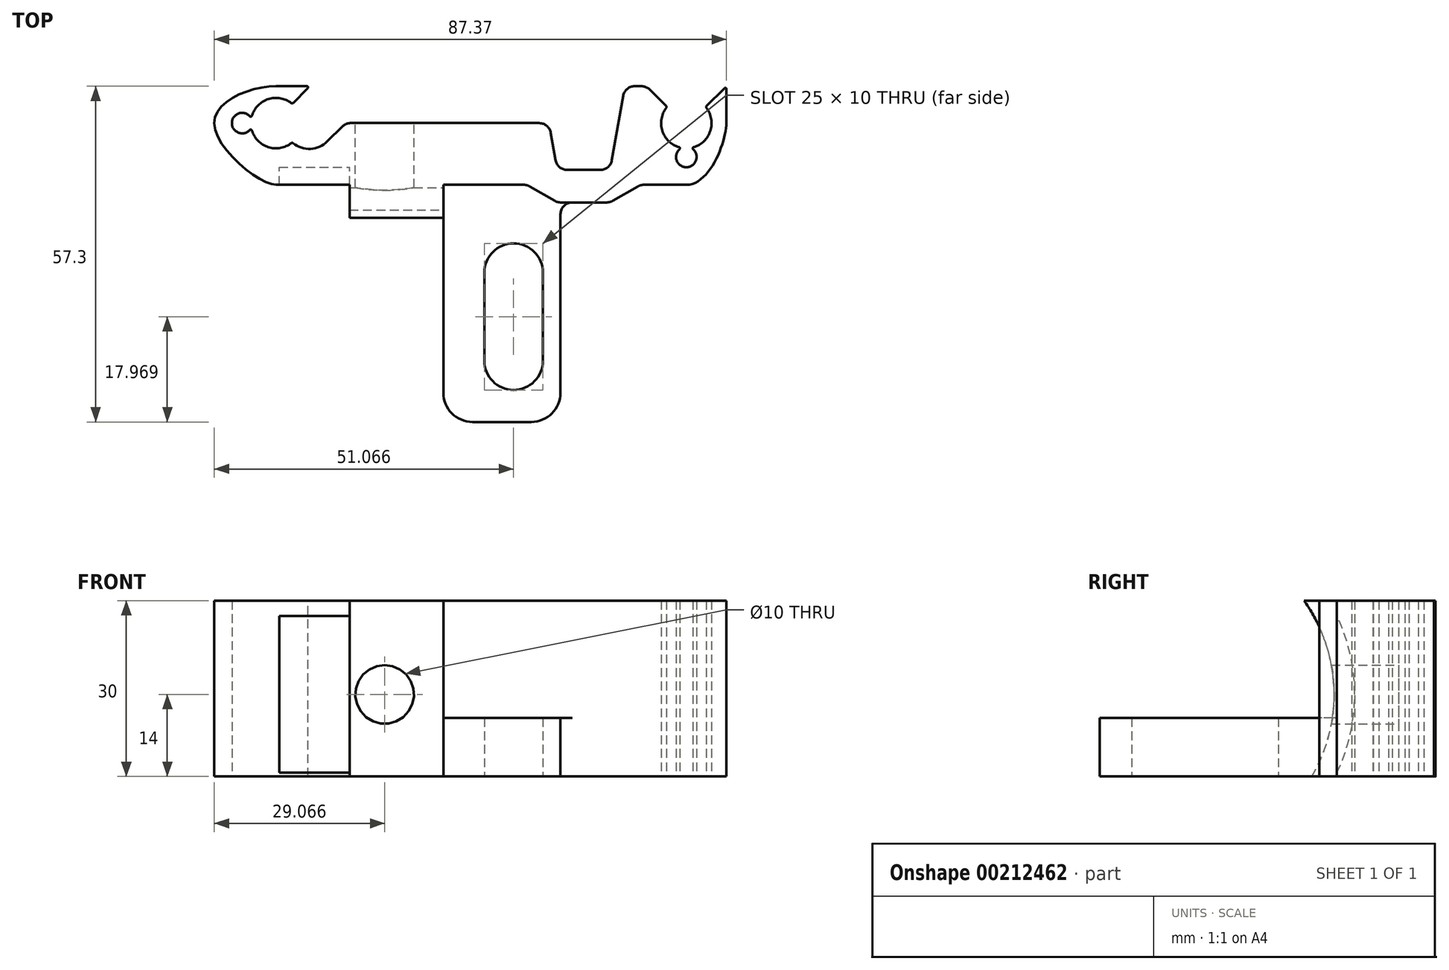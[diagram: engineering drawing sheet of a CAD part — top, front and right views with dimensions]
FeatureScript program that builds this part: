
annotation { "Feature Type Name" : "Feature", "Feature Type Description" : "" }
export const myFeature = defineFeature(function(context is Context, id is Id, definition is map)
    precondition{}
    {
        {
            var Q0;
            Q0=qCreatedBy(makeId("Top.planeOp"),FACE);
            var sketch = newSketch(context, id + "F0", { "sketchPlane" : qUnion([Q0])});
            skCircle(sketch, "E0", {"center": v(0, 0) * mm, "radius": 4.3 * mm});
            skCircle(sketch, "E1", {"center": v(5.67, 0) * mm, "radius": 4.4 * mm});
            skLineSegment(sketch, "E2", {"start": v(2.76, 3.3) * mm, "end": v(2.76, -3.3) * mm, "construction": true});
            skCircle(sketch, "E3", {"center": v(-5.78, 0) * mm, "radius": 1.75 * mm});
            skLineSegment(sketch, "E4", {"start": v(-4.22, 0.8) * mm, "end": v(-4.22, -0.8) * mm, "construction": true});
            skCircle(sketch, "E5", {"center": v(70, 0) * mm, "radius": 4.3 * mm});
            skLineSegment(sketch, "E6", {"start": v(0, 6.3) * mm, "end": v(63.16, 6.3) * mm});
            skLineSegment(sketch, "E7", {"start": v(0, -10.53) * mm, "end": v(70, -10.53) * mm});
            skFitSpline(sketch, "E8", {"points": [v(0, 6.3) * mm, v(-10.53, 0) * mm, v(0, -10.53) * mm], "startDerivative": vector(-26.26, 0) * mm, "endDerivative": vector(16.05, 0) * mm});
            skLineSegment(sketch, "E9", {"start": v(-10.53, 0) * mm, "end": v(-10.53, 6.3) * mm, "construction": true});
            skLineSegment(sketch, "E10", {"start": v(2.76, 3.3) * mm, "end": v(5.76, 6.3) * mm});
            skLineSegment(sketch, "E11", {"start": v(8.78, -3.11) * mm, "end": v(18.19, 6.3) * mm});
            skLineSegment(sketch, "E12", {"start": v(66.7, 2.76) * mm, "end": v(73.3, 2.76) * mm, "construction": true});
            skLineSegment(sketch, "E13", {"start": v(70, 0) * mm, "end": v(70, -10.53) * mm, "construction": true});
            skCircle(sketch, "E14", {"center": v(70, -5.78) * mm, "radius": 1.75 * mm});
            skLineSegment(sketch, "E15", {"start": v(69.2, -4.22) * mm, "end": v(70.8, -4.22) * mm, "construction": true});
            skLineSegment(sketch, "E16", {"start": v(73.3, 2.76) * mm, "end": v(76.84, 6.3) * mm});
            skLineSegment(sketch, "E17", {"start": v(76.84, 6.3) * mm, "end": v(76.84, 0) * mm});
            skFitSpline(sketch, "E18", {"points": [v(76.84, 0) * mm, v(70, -10.53) * mm, v(59.47, 0) * mm], "startDerivative": vector(0, -18.6) * mm, "endDerivative": vector(0, 8.99) * mm});
            skLineSegment(sketch, "E19", {"start": v(0, -4.3) * mm, "end": v(0, -10.53) * mm, "construction": true});
            skLineSegment(sketch, "E20", {"start": v(59.47, 0) * mm, "end": v(65.7, 0) * mm, "construction": true});
            skLineSegment(sketch, "E21", {"start": v(66.7, 2.76) * mm, "end": v(63.16, 6.3) * mm});
            skPoint(sketch, "E22.orphan", {"position": v(70, 6.3) * mm});
            skLineSegment(sketch, "E23", {"start": v(45.48, 6.3) * mm, "end": v(48, -8) * mm});
            skLineSegment(sketch, "E24", {"start": v(48, -8) * mm, "end": v(57, -8) * mm});
            skLineSegment(sketch, "E25", {"start": v(57, -8) * mm, "end": v(59.52, 6.3) * mm});
            skLineSegment(sketch, "E26", {"start": v(11.89, 0) * mm, "end": v(46.59, 0) * mm});
            skLineSegment(sketch, "E27", {"start": v(42.8, -10.53) * mm, "end": v(48, -13.53) * mm});
            skLineSegment(sketch, "E28", {"start": v(48, -13.53) * mm, "end": v(57, -13.53) * mm});
            skLineSegment(sketch, "E29", {"start": v(57, -13.53) * mm, "end": v(62.2, -10.53) * mm});
            skSolve(sketch);
        }
        {
            var Q0;
            {var subQ18=sQuery(id+"F0.wireOp",EDGE,"E7");Q0=makeQuery(id+"F0.imprint","IMPRINT",FACE,{"disambiguationData":[TD([[makeQuery(id+"F0.imprint","IMPRINT",EDGE,{"derivedFrom":subQ18}),1.0]])]});}
            var Q1;
            {var subQ0=sQuery(id+"F0.wireOp",EDGE,"E27");Q1=makeQuery(id+"F0.imprint","IMPRINT",FACE,{"disambiguationData":[TD([[makeQuery(id+"F0.imprint","IMPRINT",EDGE,{"derivedFrom":subQ0}),1.0]])]});}
            extrude(context, id + "F1", {"entities" : qUnion([Q0, Q1]), "depth" : 30 * mm});
        }
        {
            var Q0;
            Q0=makeQuery(id+"F1.opExtrude","SWEPT_EDGE",EDGE,{"disambiguationData":[OSD([sQuery(id+"F0.wireOp",EDGE,"E6"),sQuery(id+"F0.wireOp",EDGE,"E10")])]});
            var Q1;
            Q1=makeQuery(id+"F1.opExtrude","SWEPT_EDGE",EDGE,{"disambiguationData":[OSD([sQuery(id+"F0.wireOp",EDGE,"E0"),sQuery(id+"F0.wireOp",EDGE,"E1"),sQuery(id+"F0.wireOp",EDGE,"E10")])]});
            var Q2;
            {var subQ0=sQuery(id+"F0.wireOp",EDGE,"E3");var subQ1=sQuery(id+"F0.wireOp",EDGE,"E0");Q2=makeQuery(id+"F1.opExtrude","SWEPT_EDGE",EDGE,{"disambiguationData":[OSD([subQ1,subQ0]),TDD([makeQuery(id+"F0.imprint","INTERSECT",VERTEX,{"disambiguationData":[OD(0.0)],"derivedFrom":[subQ1,subQ0]})])]});}
            var Q3;
            {var subQ0=sQuery(id+"F0.wireOp",EDGE,"E3");var subQ1=sQuery(id+"F0.wireOp",EDGE,"E0");Q3=makeQuery(id+"F1.opExtrude","SWEPT_EDGE",EDGE,{"disambiguationData":[OSD([subQ1,subQ0]),TDD([makeQuery(id+"F0.imprint","INTERSECT",VERTEX,{"disambiguationData":[OD(1.0)],"derivedFrom":[subQ1,subQ0]})])]});}
            var Q4;
            Q4=makeQuery(id+"F1.opExtrude","SWEPT_EDGE",EDGE,{"disambiguationData":[OSD([sQuery(id+"F0.wireOp",EDGE,"E0"),sQuery(id+"F0.wireOp",EDGE,"E1")])]});
            var Q5;
            Q5=makeQuery(id+"F1.opExtrude","SWEPT_EDGE",EDGE,{"disambiguationData":[OSD([sQuery(id+"F0.wireOp",EDGE,"E16"),sQuery(id+"F0.wireOp",EDGE,"E17")])]});
            var Q6;
            Q6=makeQuery(id+"F1.opExtrude","SWEPT_EDGE",EDGE,{"disambiguationData":[OSD([sQuery(id+"F0.wireOp",EDGE,"E5"),sQuery(id+"F0.wireOp",EDGE,"E21")])]});
            var Q7;
            {var subQ0=sQuery(id+"F0.wireOp",EDGE,"E14");var subQ1=sQuery(id+"F0.wireOp",EDGE,"E5");Q7=makeQuery(id+"F1.opExtrude","SWEPT_EDGE",EDGE,{"disambiguationData":[OSD([subQ1,subQ0]),TDD([makeQuery(id+"F0.imprint","INTERSECT",VERTEX,{"disambiguationData":[OD(0.0)],"derivedFrom":[subQ1,subQ0]})])]});}
            var Q8;
            {var subQ0=sQuery(id+"F0.wireOp",EDGE,"E14");var subQ1=sQuery(id+"F0.wireOp",EDGE,"E5");Q8=makeQuery(id+"F1.opExtrude","SWEPT_EDGE",EDGE,{"disambiguationData":[OSD([subQ1,subQ0]),TDD([makeQuery(id+"F0.imprint","INTERSECT",VERTEX,{"disambiguationData":[OD(1.0)],"derivedFrom":[subQ1,subQ0]})])]});}
            var Q9;
            Q9=makeQuery(id+"F1.opExtrude","SWEPT_EDGE",EDGE,{"disambiguationData":[OSD([sQuery(id+"F0.wireOp",EDGE,"E5"),sQuery(id+"F0.wireOp",EDGE,"E16")])]});
            fillet(context, id + "F2", {"entities" : qUnion([Q0, Q1, Q2, Q3, Q4, Q5, Q6, Q7, Q8, Q9]), "radius" : .2 * mm, "tangentPropagation" : true, "allowEdgeOverflow" : false});
        }
        {
            var Q0;
            Q0=makeQuery(id+"F1.opExtrude","SWEPT_EDGE",EDGE,{"disambiguationData":[OSD([sQuery(id+"F0.wireOp",EDGE,"E6"),sQuery(id+"F0.wireOp",EDGE,"E21")])]});
            var Q1;
            Q1=makeQuery(id+"F1.opExtrude","SWEPT_EDGE",EDGE,{"disambiguationData":[OSD([sQuery(id+"F0.wireOp",EDGE,"E23"),sQuery(id+"F0.wireOp",EDGE,"E24")])]});
            var Q2;
            Q2=makeQuery(id+"F1.opExtrude","SWEPT_EDGE",EDGE,{"disambiguationData":[OSD([sQuery(id+"F0.wireOp",EDGE,"E6"),sQuery(id+"F0.wireOp",EDGE,"E25")])]});
            var Q3;
            Q3=makeQuery(id+"F1.opExtrude","SWEPT_EDGE",EDGE,{"disambiguationData":[OSD([sQuery(id+"F0.wireOp",EDGE,"E23"),sQuery(id+"F0.wireOp",EDGE,"E26")])]});
            var Q4;
            Q4=makeQuery(id+"F1.opExtrude","SWEPT_EDGE",EDGE,{"disambiguationData":[OSD([sQuery(id+"F0.wireOp",EDGE,"E23"),sQuery(id+"F0.wireOp",EDGE,"E24")])]});
            var Q5;
            Q5=makeQuery(id+"F1.opExtrude","SWEPT_EDGE",EDGE,{"disambiguationData":[OSD([sQuery(id+"F0.wireOp",EDGE,"E24"),sQuery(id+"F0.wireOp",EDGE,"E25")])]});
            var Q6;
            Q6=makeQuery(id+"F1.opExtrude","SWEPT_EDGE",EDGE,{"disambiguationData":[OSD([sQuery(id+"F0.wireOp",EDGE,"E6"),sQuery(id+"F0.wireOp",EDGE,"E21")])]});
            var Q7;
            Q7=makeQuery(id+"F1.opExtrude","SWEPT_EDGE",EDGE,{"disambiguationData":[OSD([sQuery(id+"F0.wireOp",EDGE,"E6"),sQuery(id+"F0.wireOp",EDGE,"E25")])]});
            var Q8;
            Q8=makeQuery(id+"F1.opExtrude","SWEPT_EDGE",EDGE,{"disambiguationData":[OSD([sQuery(id+"F0.wireOp",EDGE,"E11"),sQuery(id+"F0.wireOp",EDGE,"E26")])]});
            var Q9;
            Q9=makeQuery(id+"F1.opExtrude","SWEPT_EDGE",EDGE,{"disambiguationData":[OSD([sQuery(id+"F0.wireOp",EDGE,"E7"),sQuery(id+"F0.wireOp",EDGE,"E27")])]});
            var Q10;
            Q10=makeQuery(id+"F1.opExtrude","SWEPT_EDGE",EDGE,{"disambiguationData":[OSD([sQuery(id+"F0.wireOp",EDGE,"E27"),sQuery(id+"F0.wireOp",EDGE,"E28")])]});
            var Q11;
            Q11=makeQuery(id+"F1.opExtrude","SWEPT_EDGE",EDGE,{"disambiguationData":[OSD([sQuery(id+"F0.wireOp",EDGE,"E28"),sQuery(id+"F0.wireOp",EDGE,"E29")])]});
            var Q12;
            Q12=makeQuery(id+"F1.opExtrude","SWEPT_EDGE",EDGE,{"disambiguationData":[OSD([sQuery(id+"F0.wireOp",EDGE,"E7"),sQuery(id+"F0.wireOp",EDGE,"E29")])]});
            fillet(context, id + "F3", {"entities" : qUnion([Q0, Q1, Q2, Q3, Q4, Q5, Q6, Q7, Q8, Q9, Q10, Q11, Q12]), "radius" : 2 * mm, "tangentPropagation" : true, "allowEdgeOverflow" : false});
        }
        {
            var Q0;
            Q0=makeQuery(id+"F1.opExtrude","CAP_FACE",FACE,{"disambiguationData":[OSD([sQuery(id+"F0.wireOp",EDGE,"E0"),sQuery(id+"F0.wireOp",EDGE,"E1"),sQuery(id+"F0.wireOp",EDGE,"E3"),sQuery(id+"F0.wireOp",EDGE,"E5"),sQuery(id+"F0.wireOp",EDGE,"E6"),sQuery(id+"F0.wireOp",EDGE,"E7"),sQuery(id+"F0.wireOp",EDGE,"E8"),sQuery(id+"F0.wireOp",EDGE,"E10"),sQuery(id+"F0.wireOp",EDGE,"E11"),sQuery(id+"F0.wireOp",EDGE,"E14"),sQuery(id+"F0.wireOp",EDGE,"E16"),sQuery(id+"F0.wireOp",EDGE,"E17"),sQuery(id+"F0.wireOp",EDGE,"E18"),sQuery(id+"F0.wireOp",EDGE,"E21"),sQuery(id+"F0.wireOp",EDGE,"E23"),sQuery(id+"F0.wireOp",EDGE,"E24"),sQuery(id+"F0.wireOp",EDGE,"E25"),sQuery(id+"F0.wireOp",EDGE,"E26"),sQuery(id+"F0.wireOp",EDGE,"E27"),sQuery(id+"F0.wireOp",EDGE,"E28"),sQuery(id+"F0.wireOp",EDGE,"E29")])],"isStart":true});
            var sketch = newSketch(context, id + "F4", { "sketchPlane" : qUnion([Q0])});
            skLineSegment(sketch, "E30.bottom", {"start": v(28.54, 10.53) * mm, "end": v(48.54, 10.53) * mm});
            skLineSegment(sketch, "E30.top", {"start": v(28.54, 51) * mm, "end": v(48.54, 51) * mm});
            skLineSegment(sketch, "E30.left", {"start": v(28.54, 10.53) * mm, "end": v(28.54, 51) * mm});
            skLineSegment(sketch, "E30.right", {"start": v(48.54, 10.53) * mm, "end": v(48.54, 51) * mm});
            skArc(sketch, "E31", {"start": v(45.54, 40.53) * mm, "mid": v(40.54, 45.53) * mm, "end": v(35.54, 40.53) * mm});
            skArc(sketch, "E32", {"start": v(35.54, 25.53) * mm, "mid": v(40.54, 20.53) * mm, "end": v(45.54, 25.53) * mm});
            skLineSegment(sketch, "E33", {"start": v(35.54, 40.53) * mm, "end": v(35.54, 25.53) * mm});
            skLineSegment(sketch, "E34", {"start": v(45.54, 25.53) * mm, "end": v(45.54, 40.53) * mm});
            skSolve(sketch);
        }
        {
            var Q0;
            {var subQ6=sQuery(id+"F4.wireOp",EDGE,"E30.top");Q0=makeQuery(id+"F4.imprint","IMPRINT",FACE,{"disambiguationData":[TD([[makeQuery(id+"F4.imprint","IMPRINT",EDGE,{"derivedFrom":subQ6}),-1.0]])]});}
            extrude(context, id + "F5", {"entities" : qUnion([Q0]), "operationType" : NewBodyOperationType.ADD, "oppositeDirection" : true, "depth" : 10 * mm});
        }
        {
            var Q0;
            Q0=makeQuery(id+"F5.opExtrude","SWEPT_FACE",FACE,{"disambiguationData":[OSD([sQuery(id+"F4.wireOp",EDGE,"E30.left")])]});
            cPlane(context, id + "F6", {"entities" : qUnion([Q0]), "cplaneType" : CPlaneType.OFFSET, "offset" : 10 * mm, "width" : 150 * mm, "height" : 150 * mm});
        }
        {
            var Q0;
            Q0=qCreatedBy(id+"F6.planeOp",FACE);
            var sketch = newSketch(context, id + "F7", { "sketchPlane" : qUnion([Q0])});
            skCircle(sketch, "E35", {"center": v(38.5, 14) * mm, "radius": 27.5 * mm});
            skLineSegment(sketch, "E36", {"start": v(14.83, 0) * mm, "end": v(10.53, 0) * mm});
            skLineSegment(sketch, "E37", {"start": v(10.53, 0) * mm, "end": v(10.53, 30) * mm});
            skLineSegment(sketch, "E38", {"start": v(10.53, 30) * mm, "end": v(16.13, 30) * mm});
            skSolve(sketch);
        }
        {
            var Q0;
            {var subQ0=sQuery(id+"F7.wireOp",EDGE,"E36");Q0=makeQuery(id+"F7.imprint","IMPRINT",FACE,{"disambiguationData":[TD([[makeQuery(id+"F7.imprint","IMPRINT",EDGE,{"derivedFrom":subQ0}),-1.0]])]});}
            var Q1;
            Q1=makeQuery(id+"F5.opExtrude","SWEPT_FACE",FACE,{"disambiguationData":[OSD([sQuery(id+"F4.wireOp",EDGE,"E30.left")])]});
            extrude(context, id + "F8", {"entities" : qUnion([Q0]), "operationType" : NewBodyOperationType.ADD, "depth" : 6 * mm, "hasSecondDirection" : true, "secondDirectionBound" : SecondDirectionBoundingType.UP_TO_SURFACE, "secondDirectionOppositeDirection" : true, "secondDirectionBoundEntityFace" : qUnion([Q1]), "secondDirectionDepth" : 25 * mm});
        }
        {
            var Q0;
            Q0=makeQuery(id+"F8.opExtrude","CAP_FACE",FACE,{"disambiguationData":[OSD([sQuery(id+"F7.wireOp",EDGE,"E35"),sQuery(id+"F7.wireOp",EDGE,"E36"),sQuery(id+"F7.wireOp",EDGE,"E37"),sQuery(id+"F7.wireOp",EDGE,"E38")])],"isStart":false});
            var sketch = newSketch(context, id + "F9", { "sketchPlane" : qUnion([Q0])});
            skCircle(sketch, "E39", {"center": v(38.5, 14) * mm, "radius": 31 * mm});
            skLineSegment(sketch, "E40", {"start": v(10.53, 27.37) * mm, "end": v(10.53, 0.63) * mm});
            skSolve(sketch);
        }
        {
            var Q0;
            {var subQ0=sQuery(id+"F9.wireOp",EDGE,"E40");Q0=makeQuery(id+"F9.imprint","IMPRINT",FACE,{"disambiguationData":[TD([[makeQuery(id+"F9.imprint","IMPRINT",EDGE,{"derivedFrom":subQ0}),1.0]])]});}
            extrude(context, id + "F10", {"entities" : qUnion([Q0]), "operationType" : NewBodyOperationType.REMOVE, "depth" : 12 * mm});
        }
        {
            var Q0;
            {var subQ0=sQuery(id+"F0.wireOp",EDGE,"E7");Q0=makeQuery(id+"F1.opExtrude","SWEPT_FACE",FACE,{"disambiguationData":[OSD([subQ0]),TDD([makeQuery(id+"F0.imprint","IMPRINT",EDGE,{"disambiguationData":[TD([[makeQuery(id+"F0.imprint","INTERSECT",VERTEX,{"derivedFrom":[subQ0,sQuery(id+"F0.wireOp",EDGE,"E8")]}),-1.0]])],"derivedFrom":subQ0})])]});}
            var sketch = newSketch(context, id + "F11", { "sketchPlane" : qUnion([Q0])});
            skCircle(sketch, "E41", {"center": v(18.54, 14) * mm, "radius": 5 * mm});
            skSolve(sketch);
        }
        {
            var Q0;
            Q0=makeQuery(id+"F11.imprint","IMPRINT",FACE,{"disambiguationData":[TD([[makeQuery(id+"F11.imprint","IMPRINT",EDGE,{"derivedFrom":sQuery(id+"F11.wireOp",EDGE,"E41")}),1.0]])]});
            extrude(context, id + "F12", {"entities" : qUnion([Q0]), "operationType" : NewBodyOperationType.REMOVE, "endBound" : BoundingType.THROUGH_ALL, "depth" : 25 * mm, "hasSecondDirection" : true, "secondDirectionBound" : SecondDirectionBoundingType.THROUGH_ALL, "secondDirectionOppositeDirection" : true, "secondDirectionDepth" : 25 * mm});
        }
        {
            var Q0;
            {var subQ0=sQuery(id+"F0.wireOp",EDGE,"E28");var subQ1=sQuery(id+"F0.wireOp",EDGE,"E27");Q0=makeQuery(id+"F5.boolean.opBoolean","MERGE",EDGE,{"derivedFrom":[makeQuery(id+"F3.opFillet","BLEND_EDGE",EDGE,{"blendedFrom":[makeQuery(id+"F1.opExtrude","SWEPT_EDGE",EDGE,{"disambiguationData":[OSD([subQ1,subQ0])]}),makeQuery(id+"F1.opExtrude","SWEPT_FACE",FACE,{"disambiguationData":[OSD([subQ0])]})],"blendedInto":[makeQuery(id+"F1.opExtrude","SWEPT_FACE",FACE,{"disambiguationData":[OSD([subQ0])]})]}),makeQuery(id+"F5.opExtrude","SWEPT_EDGE",EDGE,{"disambiguationData":[OSD([sQuery(id+"F0.wireOp",EDGE,"E0"),sQuery(id+"F0.wireOp",EDGE,"E1"),sQuery(id+"F0.wireOp",EDGE,"E3"),sQuery(id+"F0.wireOp",EDGE,"E5"),sQuery(id+"F0.wireOp",EDGE,"E6"),sQuery(id+"F0.wireOp",EDGE,"E7"),sQuery(id+"F0.wireOp",EDGE,"E8"),sQuery(id+"F0.wireOp",EDGE,"E10"),sQuery(id+"F0.wireOp",EDGE,"E11"),sQuery(id+"F0.wireOp",EDGE,"E14"),sQuery(id+"F0.wireOp",EDGE,"E16"),sQuery(id+"F0.wireOp",EDGE,"E17"),sQuery(id+"F0.wireOp",EDGE,"E18"),sQuery(id+"F0.wireOp",EDGE,"E21"),sQuery(id+"F0.wireOp",EDGE,"E23"),sQuery(id+"F0.wireOp",EDGE,"E24"),sQuery(id+"F0.wireOp",EDGE,"E25"),sQuery(id+"F0.wireOp",EDGE,"E26"),subQ1,subQ0,sQuery(id+"F0.wireOp",EDGE,"E29"),sQuery(id+"F4.wireOp",EDGE,"E30.right")])]})]});}
            fillet(context, id + "F13", {"entities" : qUnion([Q0]), "radius" : 2 * mm, "tangentPropagation" : true, "allowEdgeOverflow" : false});
        }
        {
            var Q0;
            Q0=makeQuery(id+"F5.opExtrude","SWEPT_EDGE",EDGE,{"disambiguationData":[OSD([sQuery(id+"F4.wireOp",EDGE,"E30.top"),sQuery(id+"F4.wireOp",EDGE,"E30.left")])]});
            var Q1;
            Q1=makeQuery(id+"F5.opExtrude","SWEPT_EDGE",EDGE,{"disambiguationData":[OSD([sQuery(id+"F4.wireOp",EDGE,"E30.top"),sQuery(id+"F4.wireOp",EDGE,"E30.right")])]});
            fillet(context, id + "F14", {"entities" : qUnion([Q0, Q1]), "radius" : 5 * mm, "tangentPropagation" : true, "allowEdgeOverflow" : false});
        }
    });
